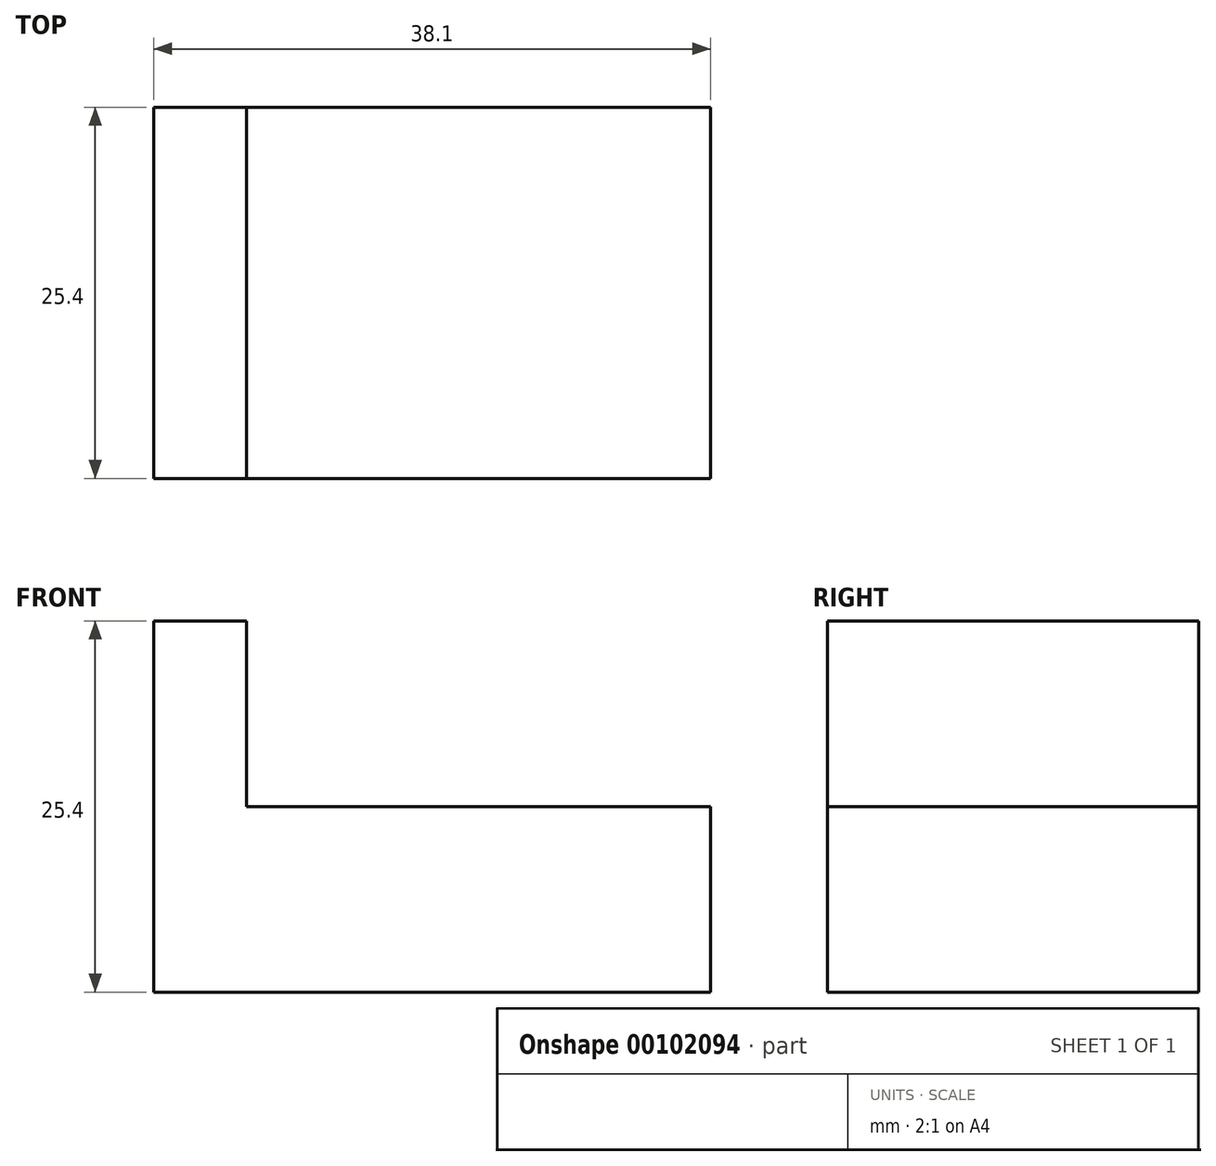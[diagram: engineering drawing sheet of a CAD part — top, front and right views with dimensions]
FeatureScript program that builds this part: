
annotation { "Feature Type Name" : "Feature", "Feature Type Description" : "" }
export const myFeature = defineFeature(function(context is Context, id is Id, definition is map)
    precondition{}
    {
        {
            var Q0;
            Q0=qCreatedBy(makeId("Front.planeOp"),FACE);
            var sketch = newSketch(context, id + "F0", { "sketchPlane" : qUnion([Q0])});
            skLineSegment(sketch, "E0", {"start": v(0, 25.4) * mm, "end": v(0, 0) * mm});
            skLineSegment(sketch, "E1", {"start": v(0, 0) * mm, "end": v(38.1, 0) * mm});
            skLineSegment(sketch, "E2", {"start": v(38.1, 0) * mm, "end": v(38.1, 12.7) * mm});
            skLineSegment(sketch, "E3", {"start": v(38.1, 12.7) * mm, "end": v(6.35, 12.7) * mm});
            skLineSegment(sketch, "E4", {"start": v(6.35, 12.7) * mm, "end": v(6.35, 25.4) * mm});
            skLineSegment(sketch, "E5", {"start": v(6.35, 25.4) * mm, "end": v(0, 25.4) * mm});
            skSolve(sketch);
        }
        {
            var Q0;
            Q0 = qSketchRegion(id + "F0", true);
            extrude(context, id + "F1", {"entities" : qUnion([Q0]), "depth" : 25.4 * mm});
        }
    });
